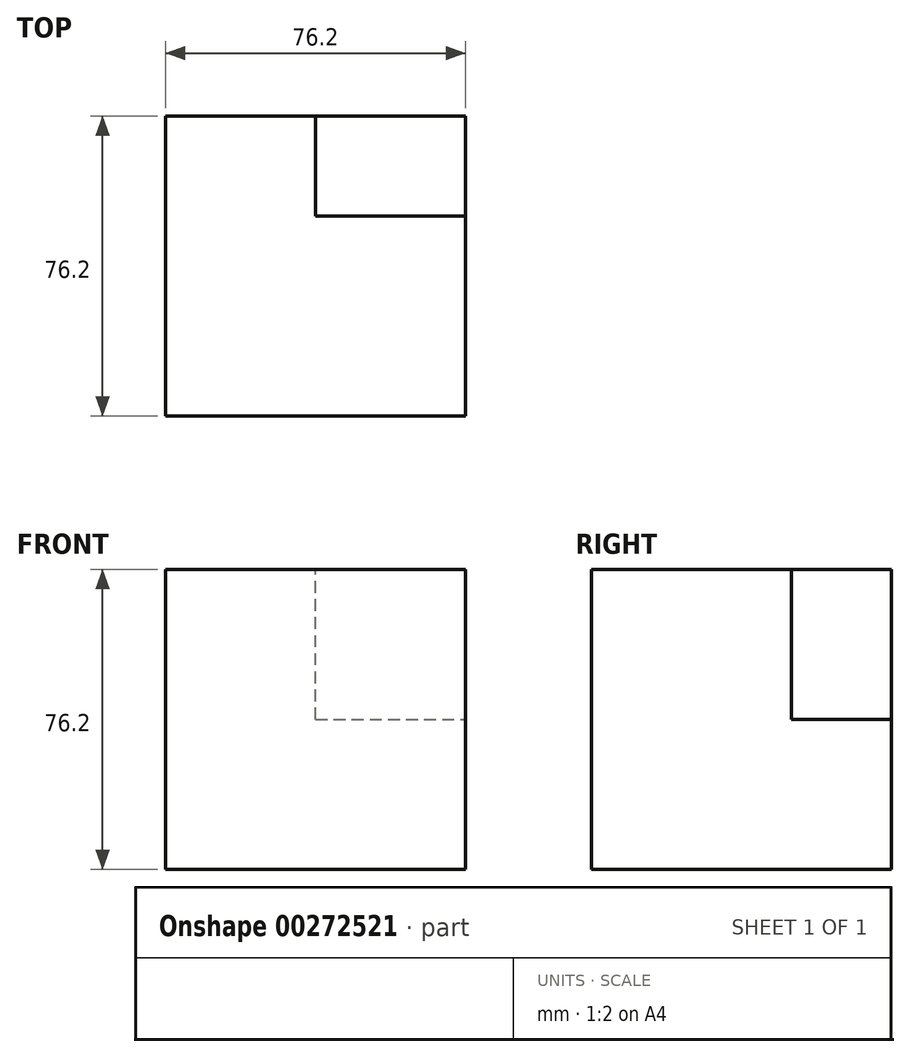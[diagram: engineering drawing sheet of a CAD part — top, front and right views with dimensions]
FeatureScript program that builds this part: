
annotation { "Feature Type Name" : "Feature", "Feature Type Description" : "" }
export const myFeature = defineFeature(function(context is Context, id is Id, definition is map)
    precondition{}
    {
        {
            var Q0;
            Q0=qCreatedBy(makeId("Front.planeOp"),FACE);
            var sketch = newSketch(context, id + "F0", { "sketchPlane" : qUnion([Q0])});
            skLineSegment(sketch, "E0.bottom", {"start": v(-38.1, 38.1) * mm, "end": v(38.1, 38.1) * mm});
            skLineSegment(sketch, "E0.top", {"start": v(-38.1, -38.1) * mm, "end": v(38.1, -38.1) * mm});
            skLineSegment(sketch, "E0.left", {"start": v(-38.1, 38.1) * mm, "end": v(-38.1, -38.1) * mm});
            skLineSegment(sketch, "E0.right", {"start": v(38.1, 38.1) * mm, "end": v(38.1, -38.1) * mm});
            skPoint(sketch, "E0.middle", {"position": v(0, 0) * mm});
            skSolve(sketch);
        }
        {
            var Q0;
            Q0 = qSketchRegion(id + "F0", true);
            extrude(context, id + "F1", {"entities" : qUnion([Q0]), "depth" : 76.2 * mm});
        }
        {
            var Q0;
            Q0=makeQuery(id+"F1.opExtrude","CAP_FACE",FACE,{"disambiguationData":[OSD([sQuery(id+"F0.wireOp",EDGE,"E0.bottom"),sQuery(id+"F0.wireOp",EDGE,"E0.top"),sQuery(id+"F0.wireOp",EDGE,"E0.left"),sQuery(id+"F0.wireOp",EDGE,"E0.right")])],"isStart":true});
            var sketch = newSketch(context, id + "F2", { "sketchPlane" : qUnion([Q0])});
            skLineSegment(sketch, "E1.bottom", {"start": v(0, 0) * mm, "end": v(-38.1, 0) * mm});
            skLineSegment(sketch, "E1.top", {"start": v(0, 38.1) * mm, "end": v(-38.1, 38.1) * mm});
            skLineSegment(sketch, "E1.left", {"start": v(0, 0) * mm, "end": v(0, 38.1) * mm});
            skLineSegment(sketch, "E1.right", {"start": v(-38.1, 0) * mm, "end": v(-38.1, 38.1) * mm});
            skSolve(sketch);
        }
        {
            var Q0;
            Q0 = qSketchRegion(id + "F2", true);
            extrude(context, id + "F3", {"entities" : qUnion([Q0]), "operationType" : NewBodyOperationType.REMOVE, "oppositeDirection" : true, "depth" : 25.4 * mm});
        }
    });
